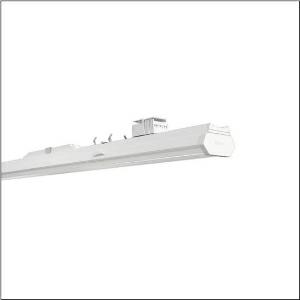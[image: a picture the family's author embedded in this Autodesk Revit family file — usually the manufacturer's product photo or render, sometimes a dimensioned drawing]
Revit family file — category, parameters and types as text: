
# Revit family: licross_r__21_protected_mo_52tp117n485g_3f7e
name_source: partatom
category: Lighting Fixtures
units: mm (PartAtom-declared; Revit-internal decimal feet)

## family parameters
Cut with Voids When Loaded = No
Host = Face
Light Source = No
Part Type = Normal
Room Calculation Point = No
Round Connector Dimension = Use Diameter
Shared = No

## types (1)
- Licross® 21 Protected MO (1 x LED, 8570 lm, 47.9 W, 4000K)
    Apparent Load = 48 VA
    CIE Flux Codes = 83 94 98 100 100
    Color Rendering = 80
    Color Temperature = 4000K
    Default Elevation = 1800 mm
    Description = Licross® 21 Protected MO, luminaire insert, of sheet steel, galvanised, coil coated, white, length: 1.500mm, width: 66mm, height: 67mm, LED rated luminous flux: 8.570lm, light colour: 840, control gear: ON/OFF, with plug, 3-pole, with phase selection, mains connection: 220..240V, AC, 50/60Hz, rated input power: 48W, halogen-free wiring, primary light control with lens, of plastic, primary optical cover: cover, of PMMA, light emission: direct distribution, primary light characteristic: symmetric, protection rating (complete): IP64, insulation class (complete): insulation class I (protective earthing), certification: CE, ENEC, VDE, UKCA, protection symbol: D if used in an environment with conductive dust loads with corresponding accessories, impact resistance: IK06, permissible ambient temperature for indoor applications: -35..+45°C, corresponds to IFS (International Featured Standards) requirements for safety and quality in the food industry, reducing of maximum allowable ambient temperature of 5°C with ceiling mounting, LABS conformity tested according to VDMA 24364:2018-05, packaging unit: 1 piece
    Height = 92 mm
    Lamp = 1 x LED
    Lamp Light Flux = 8570 lm
    Lamp Power = 47.9 W
    Lamp count = 1
    Length = 1500 mm
    Luminous efficacy = 179 lm/W
    Manufacturer = Siteco
    ModVariant = No
    Model = 52TP117N485G
    Mounting Place = Ceiling
    Mounting Type = Pendant
    Number of Poles = 1
    OnlyDefault = Yes
    Power Factor = 1
    Product Name = Licross® 21 Protected MO
    Product group = luminaire insert
    ProductGroupID = 902
    Protection Class = Protection class I
    Protection Degree = IP 64
    RLX_Detail_Level = 1
    RLX_Emergency_Light_Flux = 0 lm
    RLX_Emergency_Type = 0
    RLX_Emergency_Type_DB = No
    RlxData = <blob elided: 20401 chars, md5=5627bab6>
    Socket = socket
    Standby Power = 0 W
    System Light Flux = 8570 lm
    System Power = 48 W
    Type Comments = Product without accessories
    Type Image = l_1256148.jpg
    URL = http://relux.com
    VarID = ---
    Voltage = 0 V
    Weight = 0.00 kg
    Width = 88 mm

## geometry (parser evidence)
native form markers: Blend x4, Sweep x11
no freeform markers — native parametric forms only
